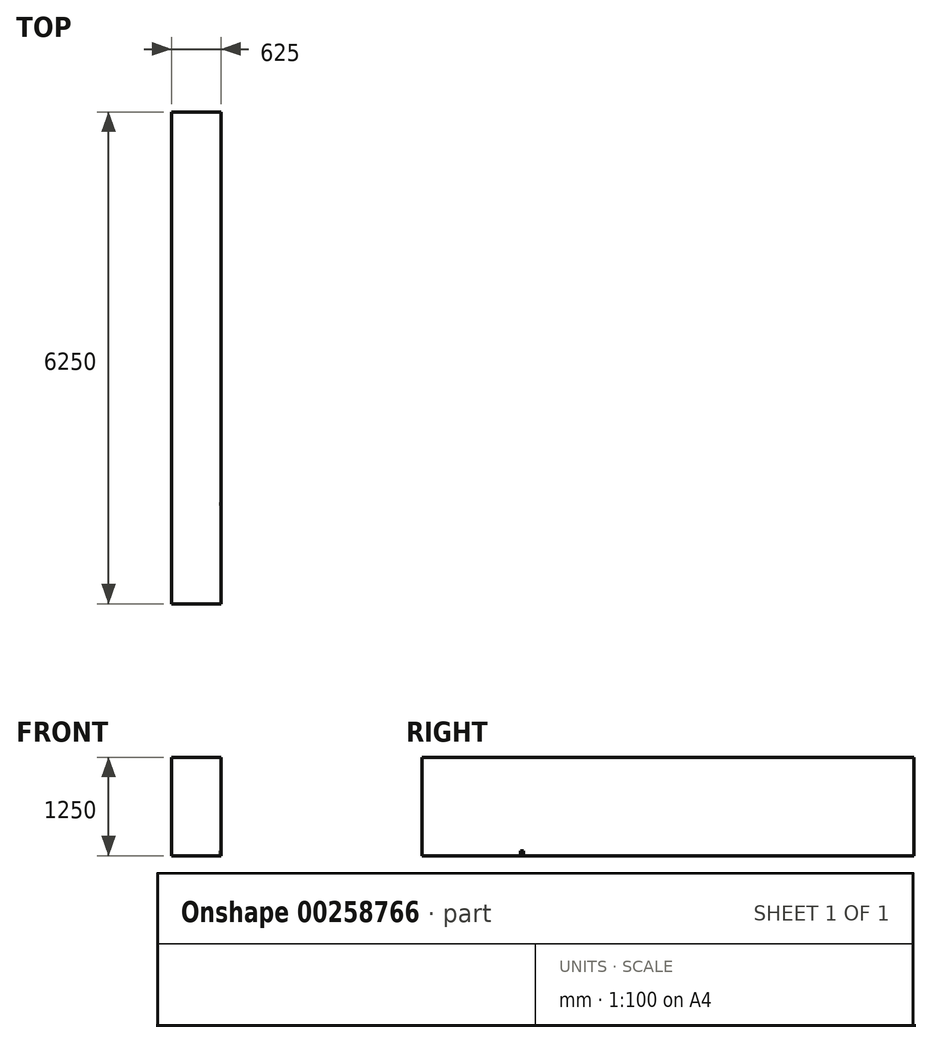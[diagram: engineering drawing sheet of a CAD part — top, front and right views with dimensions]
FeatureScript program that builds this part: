
annotation { "Feature Type Name" : "Feature", "Feature Type Description" : "" }
export const myFeature = defineFeature(function(context is Context, id is Id, definition is map)
    precondition{}
    {
        {
            var Q0;
            Q0=qCreatedBy(makeId("Front.planeOp"),FACE);
            var sketch = newSketch(context, id + "F0", { "sketchPlane" : qUnion([Q0])});
            skLineSegment(sketch, "E0", {"start": v(0, 0) * mm, "end": v(-625, 0) * mm});
            skLineSegment(sketch, "E1", {"start": v(-625, 0) * mm, "end": v(-625, 1250) * mm});
            skLineSegment(sketch, "E2", {"start": v(-625, 1250) * mm, "end": v(0, 1250) * mm});
            skLineSegment(sketch, "E3", {"start": v(0, 1250) * mm, "end": v(0, 0) * mm});
            skSolve(sketch);
        }
        {
            var Q0;
            Q0=makeQuery(id+"F0.imprint","IMPRINT",FACE,{"disambiguationData":[TD([[makeQuery(id+"F0.imprint","IMPRINT",EDGE,{"derivedFrom":sQuery(id+"F0.wireOp",EDGE,"E0")}),-1.0]])]});
            extrude(context, id + "F1", {"entities" : qUnion([Q0]), "oppositeDirection" : true, "depth" : 5000 * mm});
        }
        {
            var Q0;
            Q0=qCreatedBy(makeId("Front.planeOp"),FACE);
            var sketch = newSketch(context, id + "F2", { "sketchPlane" : qUnion([Q0])});
            skLineSegment(sketch, "E4", {"start": v(0, 0) * mm, "end": v(-19, 0) * mm});
            skLineSegment(sketch, "E5", {"start": v(-19, 0) * mm, "end": v(-19, 60) * mm});
            skLineSegment(sketch, "E6", {"start": v(-19, 60) * mm, "end": v(0, 60) * mm});
            skLineSegment(sketch, "E7", {"start": v(0, 60) * mm, "end": v(0, 0) * mm});
            skSolve(sketch);
        }
        {
            var Q0;
            Q0 = qSketchRegion(id + "F2", true);
            extrude(context, id + "F3", {"entities" : qUnion([Q0]), "operationType" : NewBodyOperationType.REMOVE, "oppositeDirection" : true, "depth" : 38.2 * mm});
        }
        {
            var Q0;
            Q0 = qSketchRegion(id + "F0", true);
            extrude(context, id + "F4", {"entities" : qUnion([Q0]), "operationType" : NewBodyOperationType.ADD, "depth" : 1250 * mm});
        }
    });
